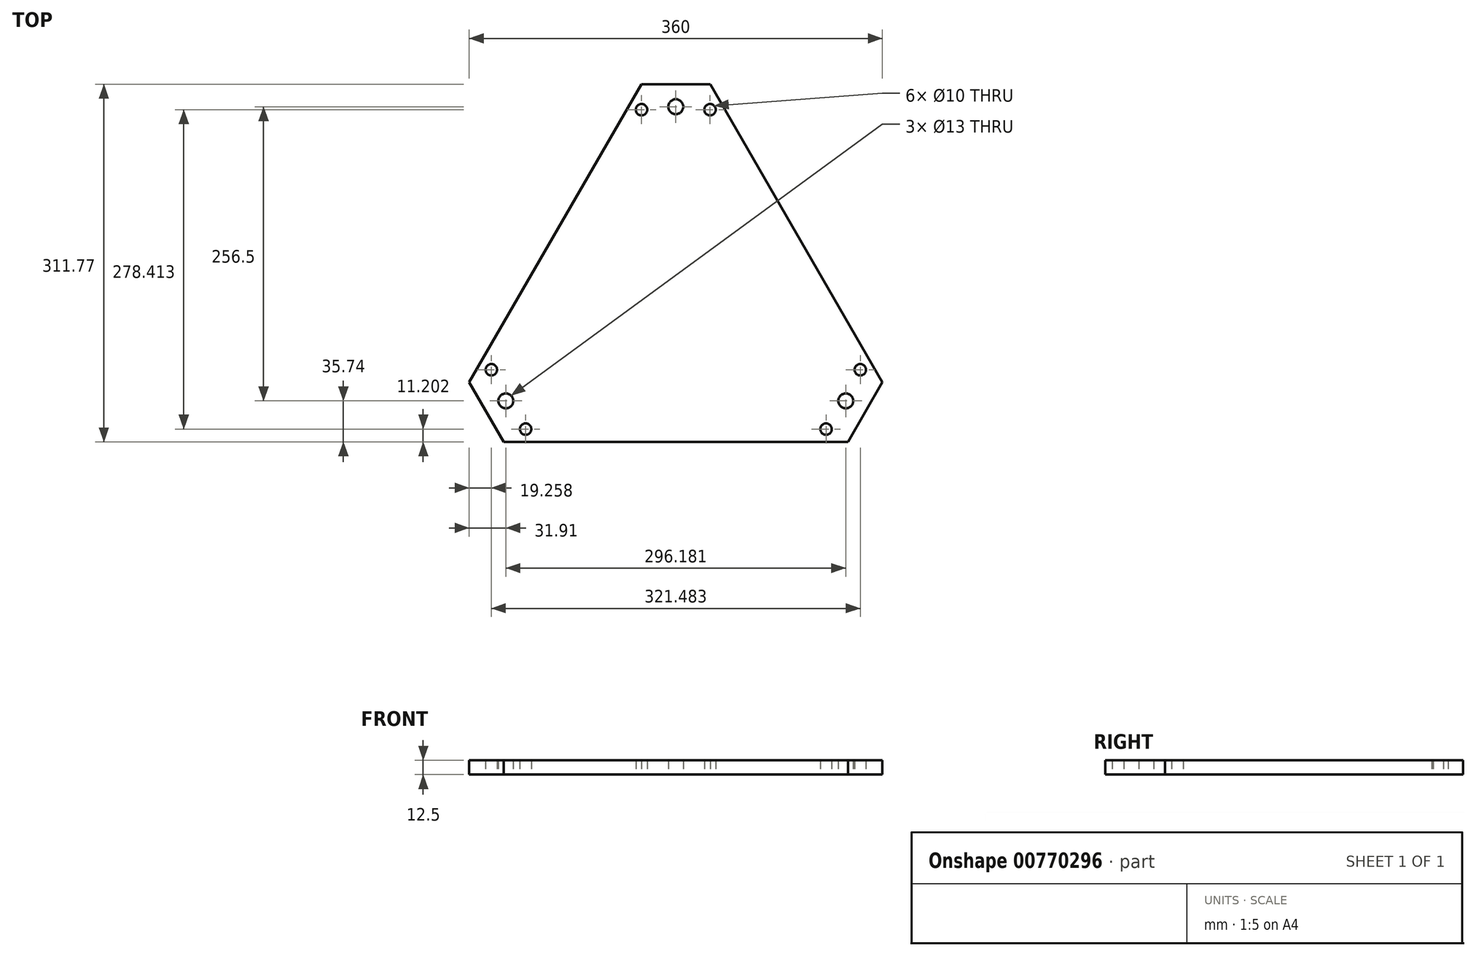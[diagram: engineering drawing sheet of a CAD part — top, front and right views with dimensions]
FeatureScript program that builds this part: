
annotation { "Feature Type Name" : "Feature", "Feature Type Description" : "" }
export const myFeature = defineFeature(function(context is Context, id is Id, definition is map)
    precondition{}
    {
        {
            var Q0;
            Q0=qCreatedBy(makeId("Top.planeOp"),FACE);
            var sketch = newSketch(context, id + "F0", { "sketchPlane" : qUnion([Q0])});
            skPoint(sketch, "E0", {"position": v(0, 0) * mm});
            skCircle(sketch, "E1", {"center": v(0, 0) * mm, "radius": 171 * mm, "construction": true});
            skLineSegment(sketch, "E2", {"start": v(0, 0) * mm, "end": v(0, 171) * mm, "construction": true});
            skLineSegment(sketch, "E3", {"start": v(0, 0) * mm, "end": v(148.1, -85.5) * mm, "construction": true});
            skLineSegment(sketch, "E4", {"start": v(0, 0) * mm, "end": v(-148.1, -85.5) * mm, "construction": true});
            skCircle(sketch, "E5", {"center": v(-148.1, -85.5) * mm, "radius": 6.5 * mm});
            skCircle(sketch, "E6", {"center": v(-160.74, -58.34) * mm, "radius": 5 * mm});
            skCircle(sketch, "E7", {"center": v(-130.9, -110.04) * mm, "radius": 5 * mm});
            skLineSegment(sketch, "E8", {"start": v(0, 0) * mm, "end": v(-160.74, -58.34) * mm, "construction": true});
            skLineSegment(sketch, "E9", {"start": v(0, 0) * mm, "end": v(-130.9, -110.04) * mm, "construction": true});
            skCircle(sketch, "E10.1.0", {"center": v(130.9, -110.04) * mm, "radius": 5 * mm});
            skCircle(sketch, "E10.1.1", {"center": v(148.1, -85.5) * mm, "radius": 6.5 * mm});
            skCircle(sketch, "E10.1.2", {"center": v(160.74, -58.34) * mm, "radius": 5 * mm});
            skLineSegment(sketch, "E10.1.3", {"start": v(0, 0) * mm, "end": v(160.74, -58.34) * mm, "construction": true});
            skLineSegment(sketch, "E10.1.5", {"start": v(0, 0) * mm, "end": v(130.9, -110.04) * mm, "construction": true});
            skCircle(sketch, "E10.2.0", {"center": v(29.85, 168.37) * mm, "radius": 5 * mm});
            skCircle(sketch, "E10.2.1", {"center": v(0, 171) * mm, "radius": 6.5 * mm});
            skCircle(sketch, "E10.2.2", {"center": v(-29.85, 168.37) * mm, "radius": 5 * mm});
            skLineSegment(sketch, "E10.2.3", {"start": v(0, 0) * mm, "end": v(-29.85, 168.37) * mm, "construction": true});
            skLineSegment(sketch, "E10.2.5", {"start": v(0, 0) * mm, "end": v(29.85, 168.37) * mm, "construction": true});
            skLineSegment(sketch, "E11", {"start": v(-180, -69.28) * mm, "end": v(-150, -121.24) * mm});
            skLineSegment(sketch, "E12", {"start": v(-150, -121.24) * mm, "end": v(150, -121.24) * mm});
            skLineSegment(sketch, "E13", {"start": v(150, -121.24) * mm, "end": v(180, -69.28) * mm});
            skLineSegment(sketch, "E14", {"start": v(180, -69.28) * mm, "end": v(30, 190.53) * mm});
            skLineSegment(sketch, "E15", {"start": v(30, 190.53) * mm, "end": v(-30, 190.53) * mm});
            skLineSegment(sketch, "E16", {"start": v(-30, 190.53) * mm, "end": v(-180, -69.28) * mm});
            skLineSegment(sketch, "E17", {"start": v(165, -95.26) * mm, "end": v(-105, 60.62) * mm, "construction": true});
            skLineSegment(sketch, "E18", {"start": v(-165, -95.26) * mm, "end": v(105, 60.62) * mm, "construction": true});
            skLineSegment(sketch, "E19", {"start": v(0, 190.53) * mm, "end": v(0, -121.24) * mm, "construction": true});
            skSolve(sketch);
        }
        {
            var Q0;
            Q0=makeQuery(id+"F0.imprint","IMPRINT",FACE,{"disambiguationData":[TD([[makeQuery(id+"F0.imprint","IMPRINT",EDGE,{"derivedFrom":sQuery(id+"F0.wireOp",EDGE,"E5")}),-1.0]])]});
            extrude(context, id + "F1", {"entities" : qUnion([Q0]), "depth" : 12.5 * mm, "offsetDistance" : 25 * mm});
        }
    });
